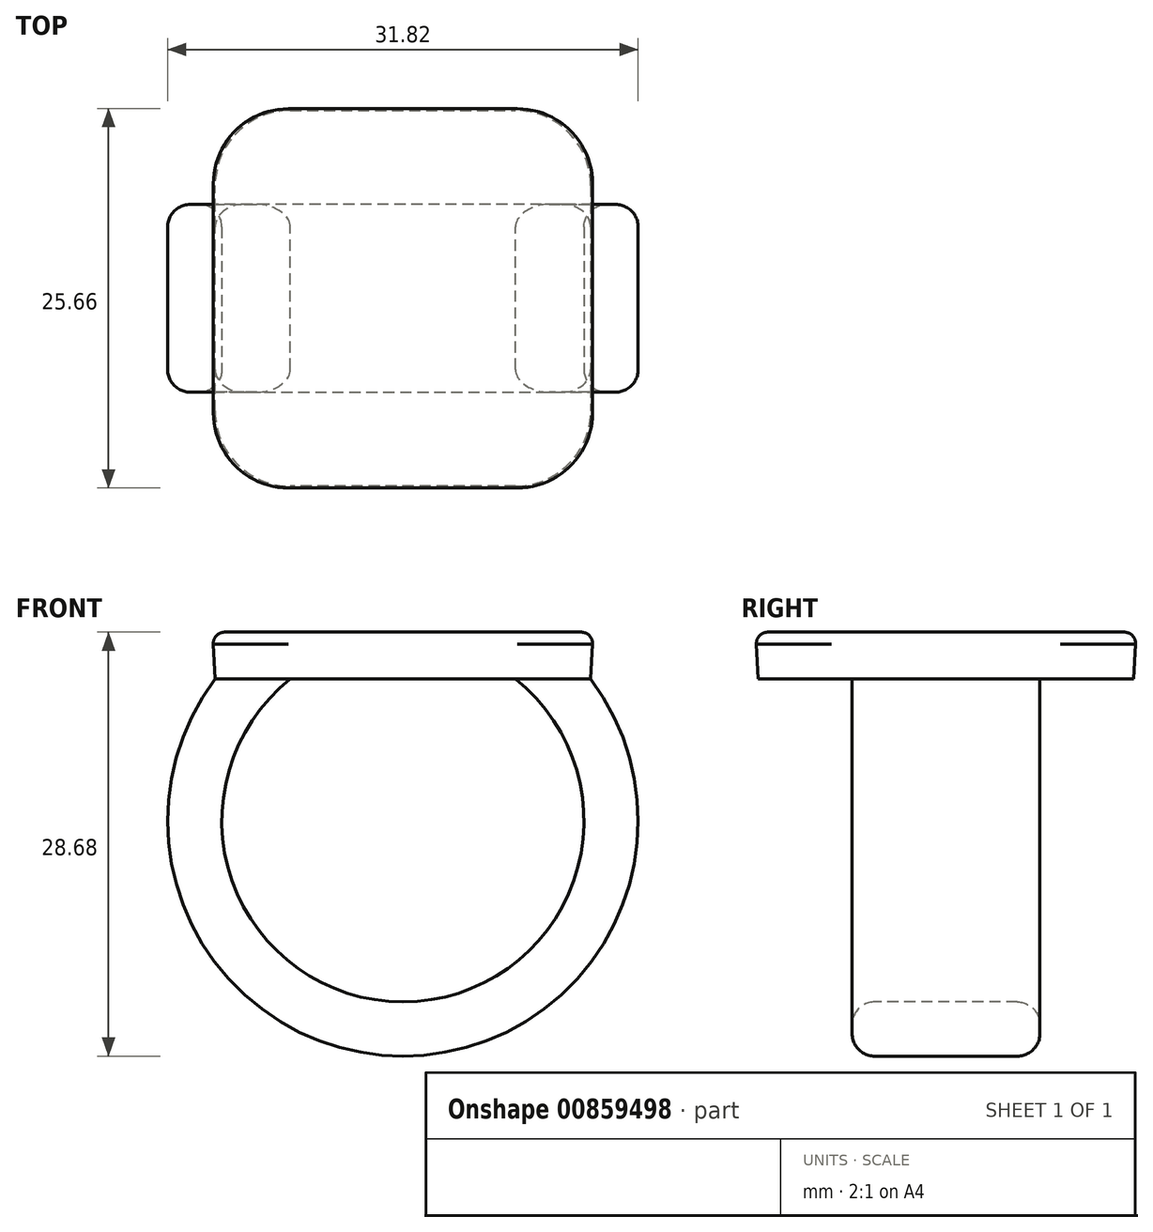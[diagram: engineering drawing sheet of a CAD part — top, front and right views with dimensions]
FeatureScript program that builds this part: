
annotation { "Feature Type Name" : "Feature", "Feature Type Description" : "" }
export const myFeature = defineFeature(function(context is Context, id is Id, definition is map)
    precondition{}
    {
        {
            var Q0;
            Q0=qCreatedBy(makeId("Top.planeOp"),FACE);
            var sketch = newSketch(context, id + "F0", { "sketchPlane" : qUnion([Q0])});
            skLineSegment(sketch, "E0.bottom", {"start": v(-12.7, 12.7) * mm, "end": v(12.7, 12.7) * mm});
            skLineSegment(sketch, "E0.top", {"start": v(-12.7, -12.7) * mm, "end": v(12.7, -12.7) * mm});
            skLineSegment(sketch, "E0.left", {"start": v(-12.7, 12.7) * mm, "end": v(-12.7, -12.7) * mm});
            skLineSegment(sketch, "E0.right", {"start": v(12.7, 12.7) * mm, "end": v(12.7, -12.7) * mm});
            skPoint(sketch, "E0.middle", {"position": v(0, 0) * mm});
            skSolve(sketch);
        }
        {
            var Q0;
            Q0 = qSketchRegion(id + "F0", true);
            extrude(context, id + "F1", {"entities" : qUnion([Q0]), "depth" : 3.17 * mm, "offsetDistance" : 25.4 * mm, "hasDraft" : true, "draftAngle" : 3 * degree});
        }
        {
            var Q0;
            Q0=qCreatedBy(makeId("Front.planeOp"),FACE);
            var sketch = newSketch(context, id + "F2", { "sketchPlane" : qUnion([Q0])});
            skArc(sketch, "E1", {"start": v(-10.16, 0) * mm, "mid": v(0, -23.56) * mm, "end": v(10.16, 0) * mm});
            skSolve(sketch);
        }
        {
            var Q0;
            Q0=makeQuery(id+"F1.opExtrude","CAP_FACE",FACE,{"disambiguationData":[OSD([sQuery(id+"F0.wireOp",EDGE,"E0.bottom"),sQuery(id+"F0.wireOp",EDGE,"E0.top"),sQuery(id+"F0.wireOp",EDGE,"E0.left"),sQuery(id+"F0.wireOp",EDGE,"E0.right")])],"isStart":true});
            var sketch = newSketch(context, id + "F3", { "sketchPlane" : qUnion([Q0])});
            skLineSegment(sketch, "E2.bottom", {"start": v(-12.7, 6.35) * mm, "end": v(-7.62, 6.35) * mm});
            skLineSegment(sketch, "E2.top", {"start": v(-12.7, -6.35) * mm, "end": v(-7.62, -6.35) * mm});
            skLineSegment(sketch, "E2.left", {"start": v(-12.7, 6.35) * mm, "end": v(-12.7, -6.35) * mm});
            skLineSegment(sketch, "E2.right", {"start": v(-7.62, 6.35) * mm, "end": v(-7.62, -6.35) * mm});
            skPoint(sketch, "E2.middle", {"position": v(-10.16, 0) * mm});
            skSolve(sketch);
        }
        {
            var Q0;
            Q0=makeQuery(id+"F3.imprint","IMPRINT",FACE,{"disambiguationData":[TD([[makeQuery(id+"F3.imprint","IMPRINT",EDGE,{"derivedFrom":sQuery(id+"F3.wireOp",EDGE,"E2.bottom")}),-1.0]])]});
            var Q1;
            Q1=sQuery(id+"F2.wireOp",EDGE,"E1");
            sweep(context, id + "F4", {"operationType" : NewBodyOperationType.ADD, "profiles" : qUnion([Q0]), "path" : qUnion([Q1])});
        }
        {
            var Q0;
            Q0=qCreatedBy(makeId("Front.planeOp"),FACE);
            var sketch = newSketch(context, id + "F5", { "sketchPlane" : qUnion([Q0])});
            skLineSegment(sketch, "E3.1", {"start": v(10.01, -2.54) * mm, "end": v(10.16, 0) * mm});
            skArc(sketch, "E3.2", {"start": v(10.01, -2.54) * mm, "mid": v(8.9, -1.18) * mm, "end": v(7.62, 0) * mm});
            skPoint(sketch, "E4.orphan", {"position": v(12.7, 0) * mm});
            skPoint(sketch, "E5.orphan", {"position": v(-7.62, 0) * mm});
            skLineSegment(sketch, "E6", {"start": v(7.62, 0) * mm, "end": v(10.16, 0) * mm});
            skPoint(sketch, "E3.0.start.orphan", {"position": v(-12.7, 0) * mm});
            skSolve(sketch);
        }
        {
            var Q0;
            Q0=makeQuery(id+"F5.imprint","IMPRINT",FACE,{"disambiguationData":[TD([[makeQuery(id+"F5.imprint","IMPRINT",EDGE,{"derivedFrom":sQuery(id+"F5.wireOp",EDGE,"E3.1")}),1.0]])]});
            var Q1;
            Q1=makeQuery(id+"F4.opSweep","SWEPT_FACE",FACE,{"disambiguationData":[OSD([sQuery(id+"F2.wireOp",EDGE,"E1"),sQuery(id+"F3.wireOp",EDGE,"E2.bottom")])]});
            var Q2;
            Q2=makeQuery(id+"F4.opSweep","SWEPT_FACE",FACE,{"disambiguationData":[OSD([sQuery(id+"F2.wireOp",EDGE,"E1"),sQuery(id+"F3.wireOp",EDGE,"E2.top")])]});
            extrude(context, id + "F6", {"entities" : qUnion([Q0]), "operationType" : NewBodyOperationType.ADD, "endBound" : BoundingType.UP_TO_SURFACE, "depth" : 25.4 * mm, "endBoundEntityFace" : qUnion([Q1]), "offsetDistance" : 25.4 * mm, "hasSecondDirection" : true, "secondDirectionBound" : SecondDirectionBoundingType.UP_TO_SURFACE, "secondDirectionOppositeDirection" : true, "secondDirectionDepth" : 25.4 * mm, "secondDirectionBoundEntityFace" : qUnion([Q2])});
        }
        {
            var Q0;
            Q0=makeQuery(id+"F1.opExtrude","SWEPT_EDGE",EDGE,{"disambiguationData":[OSD([sQuery(id+"F0.wireOp",EDGE,"E0.top"),sQuery(id+"F0.wireOp",EDGE,"E0.left")])]});
            var Q1;
            Q1=makeQuery(id+"F1.opExtrude","SWEPT_EDGE",EDGE,{"disambiguationData":[OSD([sQuery(id+"F0.wireOp",EDGE,"E0.top"),sQuery(id+"F0.wireOp",EDGE,"E0.right")])]});
            var Q2;
            Q2=makeQuery(id+"F1.opExtrude","SWEPT_EDGE",EDGE,{"disambiguationData":[OSD([sQuery(id+"F0.wireOp",EDGE,"E0.bottom"),sQuery(id+"F0.wireOp",EDGE,"E0.right")])]});
            var Q3;
            Q3=makeQuery(id+"F1.opExtrude","SWEPT_EDGE",EDGE,{"disambiguationData":[OSD([sQuery(id+"F0.wireOp",EDGE,"E0.bottom"),sQuery(id+"F0.wireOp",EDGE,"E0.left")])]});
            fillet(context, id + "F7", {"entities" : qUnion([Q0, Q1, Q2, Q3]), "radius" : 5.08 * mm, "tangentPropagation" : true, "allowEdgeOverflow" : false});
        }
        {
            var Q0;
            Q0=makeQuery(id+"F4.opSweep","SWEPT_EDGE",EDGE,{"disambiguationData":[OSD([sQuery(id+"F0.wireOp",EDGE,"E0.left"),sQuery(id+"F2.wireOp",EDGE,"E1"),sQuery(id+"F3.wireOp",EDGE,"E2.bottom"),sQuery(id+"F3.wireOp",EDGE,"E2.left")])]});
            var Q1;
            Q1=makeQuery(id+"F6.boolean.opBoolean","MERGE",EDGE,{"derivedFrom":[makeQuery(id+"F4.opSweep","SWEPT_EDGE",EDGE,{"disambiguationData":[OSD([sQuery(id+"F2.wireOp",EDGE,"E1"),sQuery(id+"F3.wireOp",EDGE,"E2.bottom"),sQuery(id+"F3.wireOp",EDGE,"E2.right")])]}),makeQuery(id+"F6.opExtrude","CAP_EDGE",EDGE,{"disambiguationData":[OSD([sQuery(id+"F5.wireOp",EDGE,"E3.2")])],"isStart":false})]});
            var Q2;
            Q2=makeQuery(id+"F4.opSweep","SWEPT_EDGE",EDGE,{"disambiguationData":[OSD([sQuery(id+"F0.wireOp",EDGE,"E0.left"),sQuery(id+"F2.wireOp",EDGE,"E1"),sQuery(id+"F3.wireOp",EDGE,"E2.top"),sQuery(id+"F3.wireOp",EDGE,"E2.left")])]});
            var Q3;
            Q3=makeQuery(id+"F6.boolean.opBoolean","MERGE",EDGE,{"derivedFrom":[makeQuery(id+"F4.opSweep","SWEPT_EDGE",EDGE,{"disambiguationData":[OSD([sQuery(id+"F2.wireOp",EDGE,"E1"),sQuery(id+"F3.wireOp",EDGE,"E2.top"),sQuery(id+"F3.wireOp",EDGE,"E2.right")])]}),makeQuery(id+"F6.opExtrude","CAP_EDGE",EDGE,{"disambiguationData":[OSD([sQuery(id+"F5.wireOp",EDGE,"E3.2")])],"isStart":true})]});
            fillet(context, id + "F8", {"entities" : qUnion([Q0, Q1, Q2, Q3]), "radius" : 1.52 * mm, "tangentPropagation" : true, "allowEdgeOverflow" : false});
        }
        {
            var Q0;
            Q0=makeQuery(id+"F1.opExtrude","CAP_FACE",FACE,{"disambiguationData":[OSD([sQuery(id+"F0.wireOp",EDGE,"E0.bottom"),sQuery(id+"F0.wireOp",EDGE,"E0.top"),sQuery(id+"F0.wireOp",EDGE,"E0.left"),sQuery(id+"F0.wireOp",EDGE,"E0.right")])],"isStart":false});
            fillet(context, id + "F9", {"entities" : qUnion([Q0]), "radius" : 0.76 * mm, "tangentPropagation" : true, "allowEdgeOverflow" : false});
        }
    });
